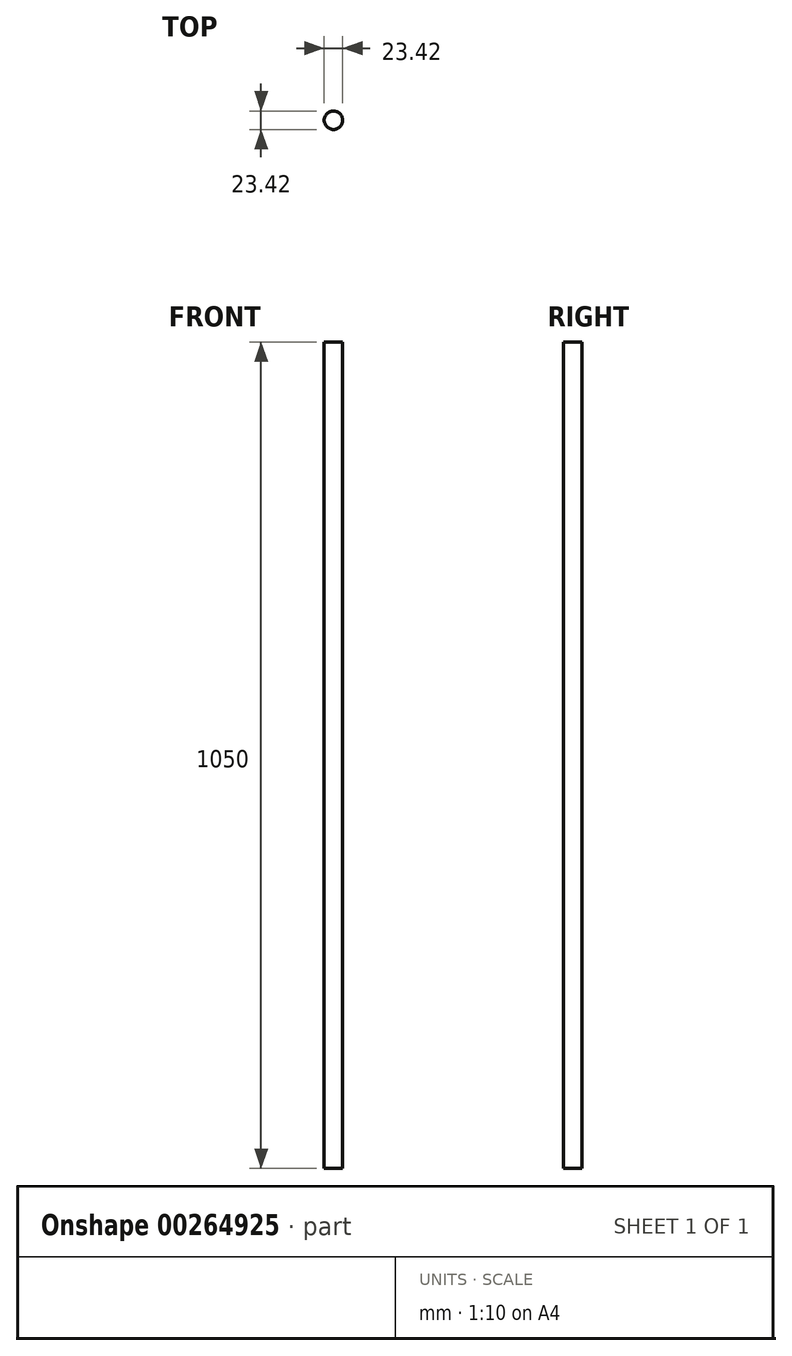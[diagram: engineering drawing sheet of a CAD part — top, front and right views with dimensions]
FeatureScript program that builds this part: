
annotation { "Feature Type Name" : "Feature", "Feature Type Description" : "" }
export const myFeature = defineFeature(function(context is Context, id is Id, definition is map)
    precondition{}
    {
        {
            var Q0;
            Q0=qCreatedBy(makeId("Top.planeOp"),FACE);
            var sketch = newSketch(context, id + "F0", { "sketchPlane" : qUnion([Q0])});
            skCircle(sketch, "E0", {"center": v(0, 0) * mm, "radius": 11.7 * mm});
            skSolve(sketch);
        }
        {
            var Q0;
            Q0 = qSketchRegion(id + "F0", true);
            extrude(context, id + "F1", {"entities" : qUnion([Q0]), "depth" : 1050 * mm});
        }
    });
